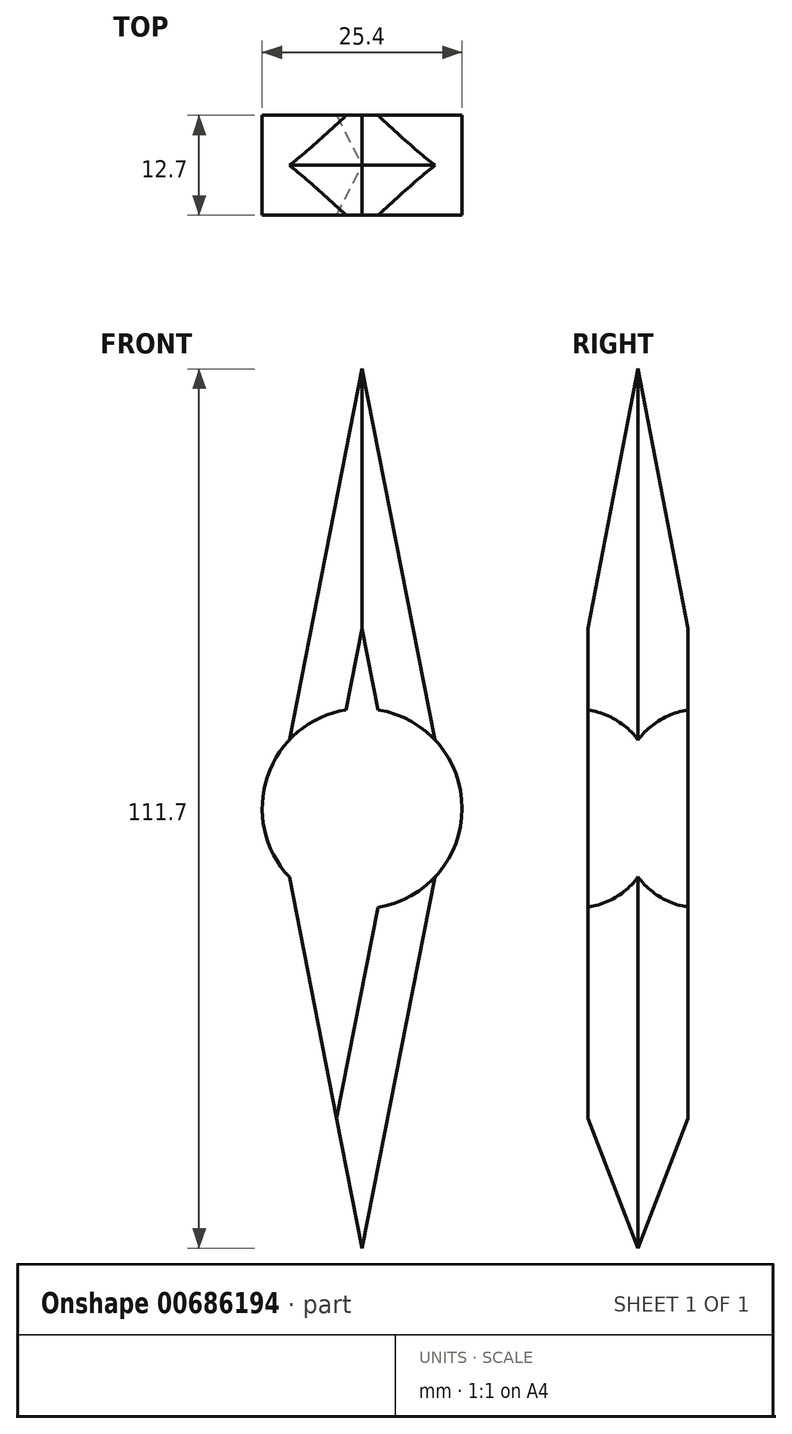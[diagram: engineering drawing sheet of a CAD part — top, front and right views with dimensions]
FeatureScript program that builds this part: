
annotation { "Feature Type Name" : "Feature", "Feature Type Description" : "" }
export const myFeature = defineFeature(function(context is Context, id is Id, definition is map)
    precondition{}
    {
        {
            var Q0;
            Q0=qCreatedBy(makeId("Front.planeOp"),FACE);
            var sketch = newSketch(context, id + "F0", { "sketchPlane" : qUnion([Q0])});
            skCircle(sketch, "E0", {"center": v(0, 0) * mm, "radius": 12.7 * mm});
            skLineSegment(sketch, "E1", {"start": v(-9.25, 8.7) * mm, "end": v(0, 55.85) * mm});
            skLineSegment(sketch, "E2", {"start": v(0, 12.7) * mm, "end": v(0, -12.7) * mm});
            skLineSegment(sketch, "E3", {"start": v(12.7, 0) * mm, "end": v(-12.7, 0) * mm});
            skLineSegment(sketch, "E4.MirrorCS", {"start": v(9.25, 8.7) * mm, "end": v(0, 55.85) * mm});
            skLineSegment(sketch, "E5.MirrorCS", {"start": v(9.25, -8.7) * mm, "end": v(0, -55.85) * mm});
            skLineSegment(sketch, "E6.MirrorCS", {"start": v(-9.25, -8.7) * mm, "end": v(0, -55.85) * mm});
            skLineSegment(sketch, "E7.MirrorCS", {"start": v(0, -12.7) * mm, "end": v(0, 12.7) * mm});
            skSolve(sketch);
        }
        {
            var Q0;
            Q0 = qSketchRegion(id + "F0", true);
            extrude(context, id + "F1", {"entities" : qUnion([Q0]), "depth" : 12.7 * mm, "offsetDistance" : 25.4 * mm});
        }
        {
            var Q0;
            Q0=makeQuery(id+"F1.opExtrude","CAP_EDGE",EDGE,{"disambiguationData":[OSD([sQuery(id+"F0.wireOp",EDGE,"E4.MirrorCS")])],"isStart":false});
            var Q1;
            Q1=makeQuery(id+"F1.opExtrude","CAP_EDGE",EDGE,{"disambiguationData":[OSD([sQuery(id+"F0.wireOp",EDGE,"E4.MirrorCS")])],"isStart":true});
            var Q2;
            Q2=makeQuery(id+"F1.opExtrude","CAP_EDGE",EDGE,{"disambiguationData":[OSD([sQuery(id+"F0.wireOp",EDGE,"E1")])],"isStart":false});
            var Q3;
            Q3=makeQuery(id+"F1.opExtrude","CAP_EDGE",EDGE,{"disambiguationData":[OSD([sQuery(id+"F0.wireOp",EDGE,"E1")])],"isStart":true});
            var Q4;
            Q4=makeQuery(id+"F1.opExtrude","CAP_EDGE",EDGE,{"disambiguationData":[OSD([sQuery(id+"F0.wireOp",EDGE,"E6.MirrorCS")])],"isStart":false});
            var Q5;
            Q5=makeQuery(id+"F1.opExtrude","CAP_EDGE",EDGE,{"disambiguationData":[OSD([sQuery(id+"F0.wireOp",EDGE,"E5.MirrorCS")])],"isStart":false});
            var Q6;
            Q6=makeQuery(id+"F1.opExtrude","CAP_EDGE",EDGE,{"disambiguationData":[OSD([sQuery(id+"F0.wireOp",EDGE,"E6.MirrorCS")])],"isStart":true});
            var Q7;
            Q7=makeQuery(id+"F1.opExtrude","CAP_EDGE",EDGE,{"disambiguationData":[OSD([sQuery(id+"F0.wireOp",EDGE,"E5.MirrorCS")])],"isStart":true});
            chamfer(context, id + "F2", {"entities" : qUnion([Q0, Q1, Q2, Q3, Q4, Q5, Q6, Q7]), "width" : 6.35 * mm, "tangentPropagation" : true});
        }
    });
